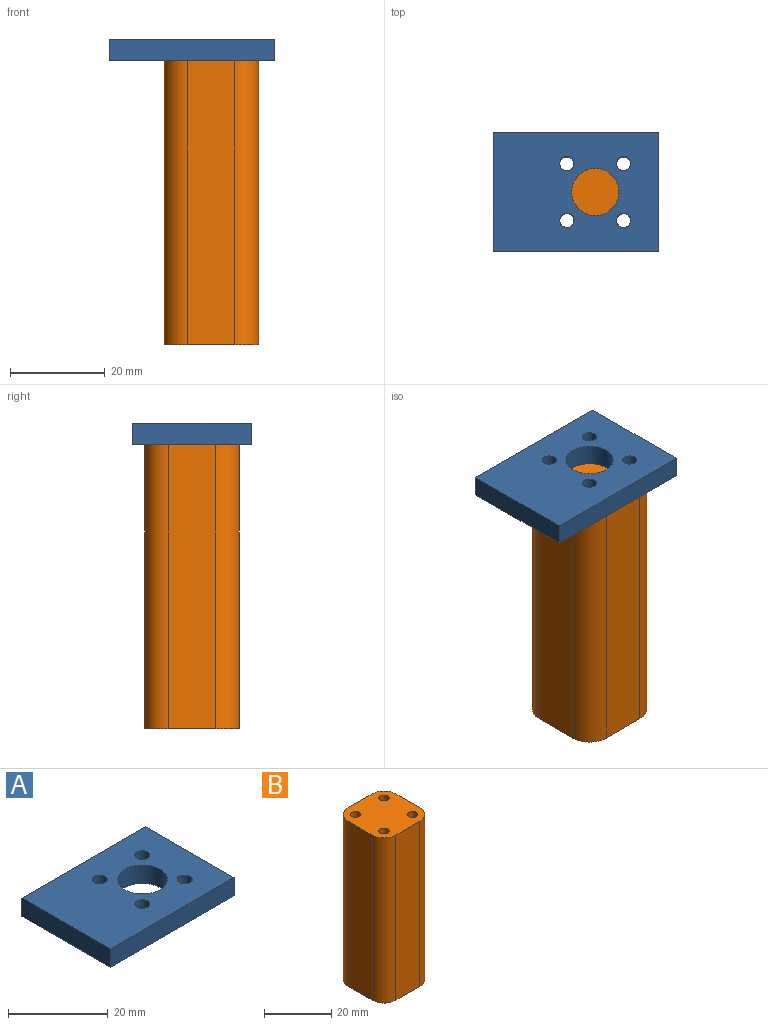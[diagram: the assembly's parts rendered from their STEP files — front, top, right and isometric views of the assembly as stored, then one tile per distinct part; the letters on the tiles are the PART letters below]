
ASSEMBLY  parts=2 mates=1
PART A: 11 faces, bbox 35x25x4.5 mm
  f0: plane 34.99x4.5mm, normal (0,1,0), area 157.5mm2, adj f1,f8,f9,f10
  f1: plane 24.99x4.5mm, normal (-1,0,0), area 112.5mm2, adj f0,f2,f9,f10
  f2: plane 35x4.5mm, normal (0,-1,0), area 157.5mm2, adj f1,f8,f9,f10
  f3: cylinder r=5mm len=10mm, axis (0,0,-1), area 141.4mm2, adj f9,f10
  f4: cylinder r=1.5mm len=4.5mm, axis (0,0,-1), area 42.4mm2, adj f9,f10
  f5: cylinder r=1.5mm len=4.5mm, axis (0,0,-1), area 42.4mm2, adj f9,f10
  f6: cylinder r=1.5mm len=4.5mm, axis (0,0,-1), area 42.4mm2, adj f9,f10
  f7: cylinder r=1.5mm len=4.5mm, axis (0,0,-1), area 42.4mm2, adj f9,f10
  f8: plane 25x4.5mm, normal (1,0,0), area 112.5mm2, adj f0,f2,f9,f10
  f9: plane 35x25mm, normal (0,0,1), area 768mm2, adj f0,f1,f2,f3,f4,f5,f6,f7
  f10: plane 35x25mm, normal (0,0,-1), area 768mm2, adj f0,f1,f2,f3,f4,f5,f6,f7
PART B: 14 faces, bbox 20x20x60 mm
  f0: plane 60x10mm, normal (0,-1,0), area 600mm2, adj f8,f9,f10,f13
  f1: plane 60x10mm, normal (1,0,0), area 600mm2, adj f8,f9,f10,f11
  f2: plane 60x10mm, normal (0,1,0), area 600mm2, adj f8,f9,f11,f12
  f3: cylinder r=1.5mm len=60mm, axis (0,0,-1), area 565.5mm2, adj f8,f9
  f4: cylinder r=1.5mm len=60mm, axis (0,0,-1), area 565.5mm2, adj f8,f9
  f5: cylinder r=1.5mm len=60mm, axis (0,0,-1), area 565.5mm2, adj f8,f9
  f6: cylinder r=1.5mm len=60mm, axis (0,0,-1), area 565.5mm2, adj f8,f9
  f7: plane 60x10mm, normal (-1,0,0), area 600mm2, adj f8,f9,f12,f13
  f8: plane 20x20mm, normal (0,0,1), area 350.3mm2, adj f0,f1,f2,f3,f4,f5,f6,f7
  f9: plane 20x20mm, normal (0,0,-1), area 350.3mm2, adj f0,f1,f2,f3,f4,f5,f6,f7
  f10: cylinder r=5mm len=60mm, axis (0,0,1), area 471.2mm2, adj f0,f1,f8,f9
  f11: cylinder r=5mm len=60mm, axis (0,0,-1), area 471.2mm2, adj f1,f2,f8,f9
  f12: cylinder r=5mm len=60mm, axis (0,0,1), area 471.2mm2, adj f2,f7,f8,f9
  f13: cylinder r=5mm len=60mm, axis (0,0,-1), area 471.2mm2, adj f0,f7,f8,f9
PLACE A t=(0,0,-5)mm
PLACE B t=(-22.93,2.57,-65)mm
MATE fastened B.f8 <-> A.f3  axis (0,0,1) through (-41.02,16.23,-5)mm
